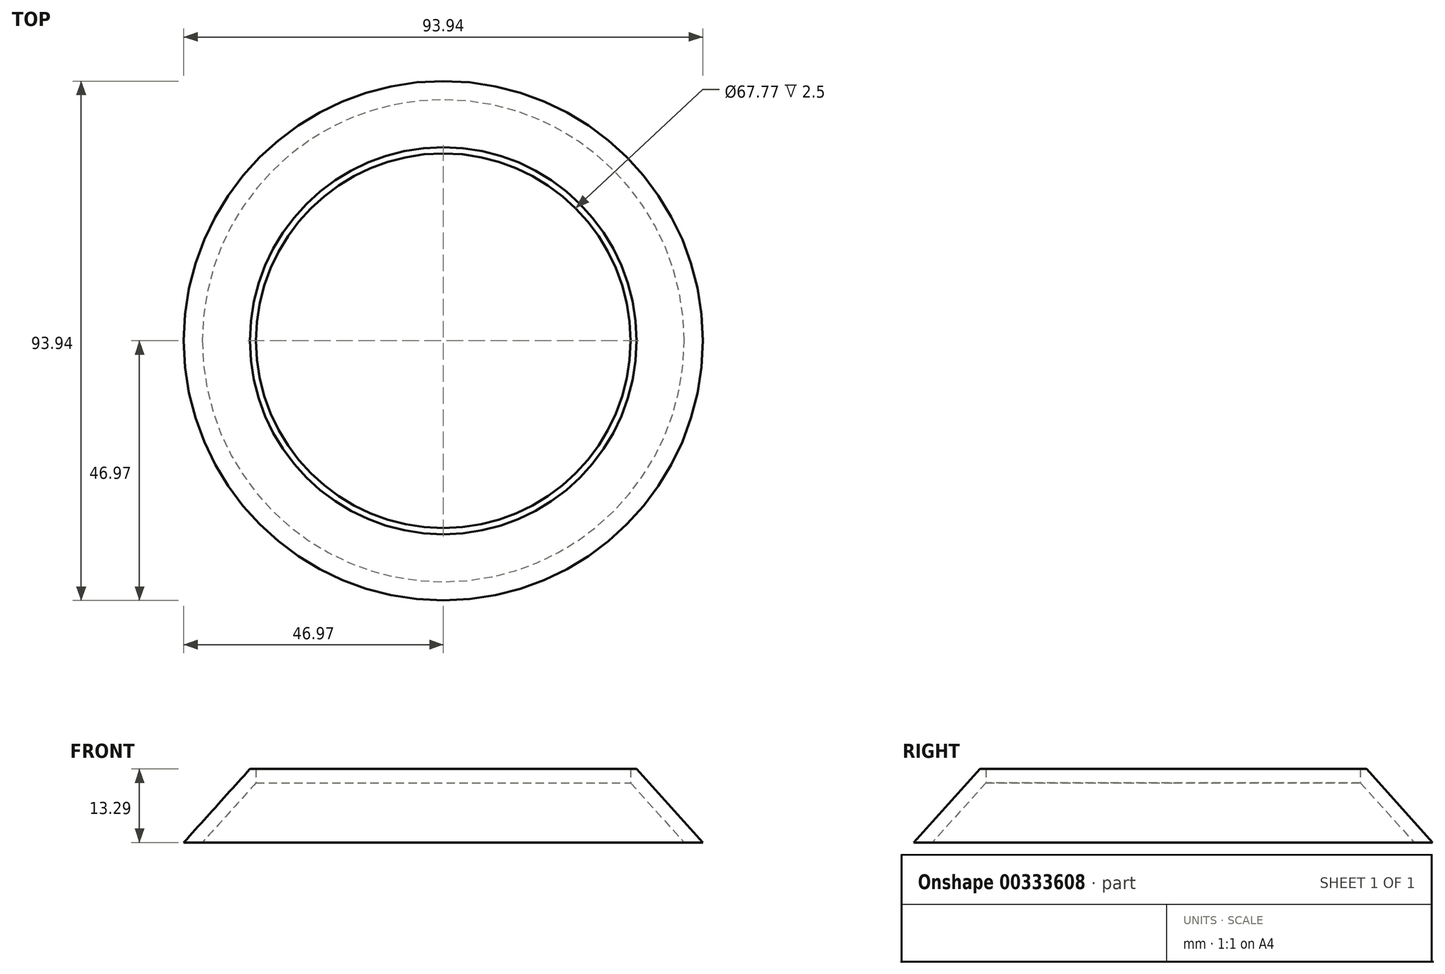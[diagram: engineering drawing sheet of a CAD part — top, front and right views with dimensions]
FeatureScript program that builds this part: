
annotation { "Feature Type Name" : "Feature", "Feature Type Description" : "" }
export const myFeature = defineFeature(function(context is Context, id is Id, definition is map)
    precondition{}
    {
        {
            var Q0;
            Q0=qCreatedBy(makeId("Front.planeOp"),FACE);
            var sketch = newSketch(context, id + "F0", { "sketchPlane" : qUnion([Q0])});
            skLineSegment(sketch, "E0", {"start": v(0, 13.29) * mm, "end": v(-35, 13.29) * mm});
            skLineSegment(sketch, "E1", {"start": v(-35, 13.29) * mm, "end": v(-46.97, 0) * mm});
            skLineSegment(sketch, "E2", {"start": v(-46.97, 0) * mm, "end": v(0, 0) * mm});
            skLineSegment(sketch, "E3", {"start": v(0, 0) * mm, "end": v(0, 13.29) * mm});
            skLineSegment(sketch, "E4", {"start": v(0, 13.29) * mm, "end": v(0, 52.16) * mm, "construction": true});
            skSolve(sketch);
        }
        {
            var Q0;
            Q0=makeQuery(id+"F0.imprint","IMPRINT",FACE,{"disambiguationData":[TD([[makeQuery(id+"F0.imprint","IMPRINT",EDGE,{"derivedFrom":sQuery(id+"F0.wireOp",EDGE,"E0")}),1.0]])]});
            var Q1;
            Q1=sQuery(id+"F0.wireOp",EDGE,"E4");
            revolve(context, id + "F1", {"entities" : qUnion([Q0]), "axis" : qUnion([Q1]), "revolveType" : RevolveType.FULL});
        }
        {
            var Q0;
            Q0=makeQuery(id+"F1.opRevolve","SWEPT_FACE",FACE,{"disambiguationData":[OSD([sQuery(id+"F0.wireOp",EDGE,"E2")])]});
            shell(context, id + "F2", {"entities" : qUnion([Q0]), "thickness" : 2.5 * mm});
        }
        {
            var Q0;
            Q0=makeQuery(id+"F2.opShell","OFFSET_FACE",FACE,{"disambiguationData":[OSD([sQuery(id+"F0.wireOp",EDGE,"E0")])]});
            extrude(context, id + "F3", {"entities" : qUnion([Q0]), "operationType" : NewBodyOperationType.ADD, "depth" : 25 * mm});
        }
        {
            var Q0;
            Q0=makeQuery(id+"F3.opExtrude","CAP_FACE",FACE,{"disambiguationData":[OSD([sQuery(id+"F0.wireOp",EDGE,"E0")])],"isStart":false});
            extrude(context, id + "F4", {"entities" : qUnion([Q0]), "operationType" : NewBodyOperationType.ADD, "oppositeDirection" : true, "depth" : 25 * mm});
        }
        {
            var Q0;
            Q0=makeQuery(id+"F3.opExtrude","CAP_FACE",FACE,{"disambiguationData":[OSD([sQuery(id+"F0.wireOp",EDGE,"E0")])],"isStart":false});
            extrude(context, id + "F5", {"entities" : qUnion([Q0]), "operationType" : NewBodyOperationType.REMOVE, "endBound" : BoundingType.THROUGH_ALL, "oppositeDirection" : true, "depth" : 25 * mm});
        }
    });
